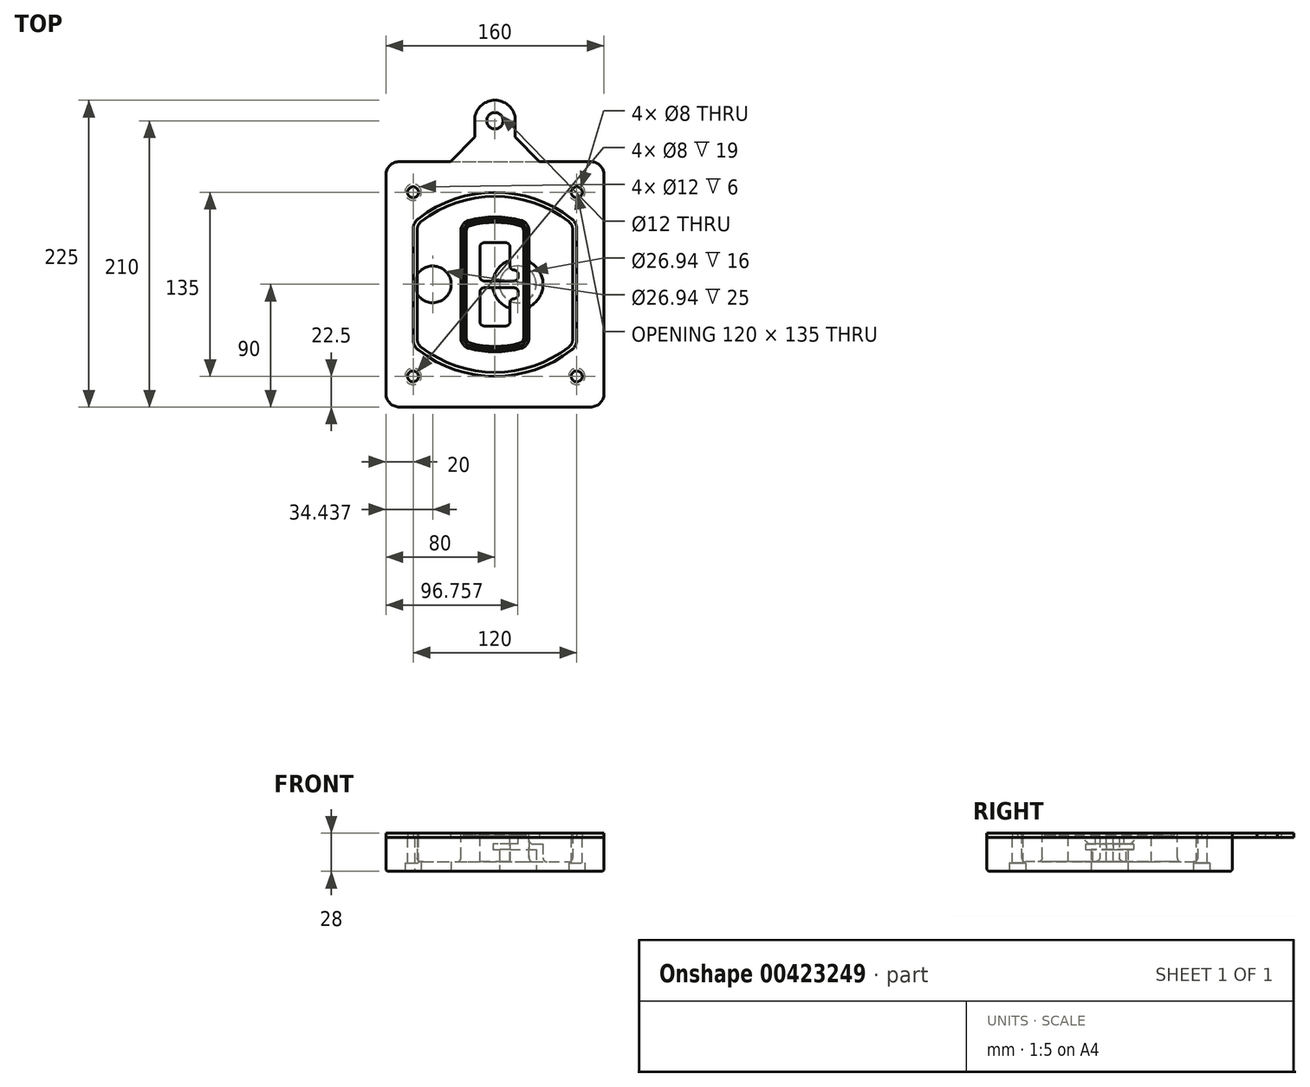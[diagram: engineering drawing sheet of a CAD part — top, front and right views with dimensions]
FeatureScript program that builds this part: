
annotation { "Feature Type Name" : "Feature", "Feature Type Description" : "" }
export const myFeature = defineFeature(function(context is Context, id is Id, definition is map)
    precondition{}
    {
        {
            var Q0;
            Q0=qCreatedBy(makeId("Top.planeOp"),FACE);
            var sketch = newSketch(context, id + "F0", { "sketchPlane" : qUnion([Q0])});
            skPoint(sketch, "E0.rect.middle", {"position": v(0, 0) * mm});
            skLineSegment(sketch, "E1.bottom", {"start": v(-70, -90) * mm, "end": v(70, -90) * mm});
            skLineSegment(sketch, "E1.top", {"start": v(-70, 90) * mm, "end": v(70, 90) * mm});
            skLineSegment(sketch, "E1.left", {"start": v(-80, -80) * mm, "end": v(-80, 80) * mm});
            skLineSegment(sketch, "E1.right", {"start": v(80, -80) * mm, "end": v(80, 80) * mm});
            skLineSegment(sketch, "E2", {"start": v(-80, 90) * mm, "end": v(80, -90) * mm, "construction": true});
            skLineSegment(sketch, "E3", {"start": v(80, 90) * mm, "end": v(-80, -90) * mm, "construction": true});
            skCircle(sketch, "E4", {"center": v(-60, 67.5) * mm, "radius": 4 * mm});
            skCircle(sketch, "E5", {"center": v(60, 67.5) * mm, "radius": 4 * mm});
            skCircle(sketch, "E6", {"center": v(60, -67.5) * mm, "radius": 4 * mm});
            skCircle(sketch, "E7", {"center": v(-60, -67.5) * mm, "radius": 4 * mm});
            skLineSegment(sketch, "E8", {"start": v(-60, 67.5) * mm, "end": v(60, 67.5) * mm, "construction": true});
            skLineSegment(sketch, "E9", {"start": v(60, 67.5) * mm, "end": v(60, -67.5) * mm, "construction": true});
            skLineSegment(sketch, "E10", {"start": v(60, -67.5) * mm, "end": v(-60, -67.5) * mm, "construction": true});
            skLineSegment(sketch, "E11", {"start": v(-60, -67.5) * mm, "end": v(-60, 67.5) * mm, "construction": true});
            skLineSegment(sketch, "E12", {"start": v(-60, 40.3) * mm, "end": v(-60, -40.3) * mm});
            skLineSegment(sketch, "E13", {"start": v(60, 40.3) * mm, "end": v(60, -40.3) * mm});
            skArc(sketch, "E14", {"start": v(56.15, 48.18) * mm, "mid": v(0, 67.5) * mm, "end": v(-56.15, 48.18) * mm});
            skArc(sketch, "E15", {"start": v(-56.15, -48.18) * mm, "mid": v(0, -67.5) * mm, "end": v(56.15, -48.18) * mm});
            skLineSegment(sketch, "E16", {"start": v(-60, 0) * mm, "end": v(60, 0) * mm, "construction": true});
            skPoint(sketch, "E17.visualSharp", {"position": v(-60, -45) * mm});
            skArc(sketch, "E17.filletArc", {"start": v(-60, -40.3) * mm, "mid": v(-58.99, -44.68) * mm, "end": v(-56.15, -48.18) * mm});
            skPoint(sketch, "E18.visualSharp", {"position": v(-60, 45) * mm});
            skArc(sketch, "E18.filletArc", {"start": v(-56.15, 48.18) * mm, "mid": v(-58.99, 44.68) * mm, "end": v(-60, 40.3) * mm});
            skPoint(sketch, "E19.visualSharp", {"position": v(60, 45) * mm});
            skArc(sketch, "E19.filletArc", {"start": v(60, 40.3) * mm, "mid": v(58.99, 44.68) * mm, "end": v(56.15, 48.18) * mm});
            skPoint(sketch, "E20.visualSharp", {"position": v(60, -45) * mm});
            skArc(sketch, "E20.filletArc", {"start": v(56.15, -48.18) * mm, "mid": v(58.99, -44.68) * mm, "end": v(60, -40.3) * mm});
            skPoint(sketch, "E21.visualSharp", {"position": v(-80, 90) * mm});
            skArc(sketch, "E21.filletArc", {"start": v(-70, 90) * mm, "mid": v(-77.07, 87.07) * mm, "end": v(-80, 80) * mm});
            skPoint(sketch, "E22.visualSharp", {"position": v(80, 90) * mm});
            skArc(sketch, "E22.filletArc", {"start": v(80, 80) * mm, "mid": v(77.07, 87.07) * mm, "end": v(70, 90) * mm});
            skPoint(sketch, "E23.visualSharp", {"position": v(80, -90) * mm});
            skArc(sketch, "E23.filletArc", {"start": v(70, -90) * mm, "mid": v(77.07, -87.07) * mm, "end": v(80, -80) * mm});
            skPoint(sketch, "E24.visualSharp", {"position": v(-80, -90) * mm});
            skArc(sketch, "E24.filletArc", {"start": v(-80, -80) * mm, "mid": v(-77.07, -87.07) * mm, "end": v(-70, -90) * mm});
            skArc(sketch, "E25.0", {"start": v(57, 40.3) * mm, "mid": v(56.3, 43.36) * mm, "end": v(54.3, 45.81) * mm});
            skLineSegment(sketch, "E25.1", {"start": v(57, 40.3) * mm, "end": v(57, -40.3) * mm});
            skArc(sketch, "E25.2", {"start": v(54.3, -45.81) * mm, "mid": v(56.3, -43.36) * mm, "end": v(57, -40.3) * mm});
            skArc(sketch, "E25.3", {"start": v(-54.3, -45.81) * mm, "mid": v(0, -64.5) * mm, "end": v(54.3, -45.81) * mm});
            skArc(sketch, "E25.4", {"start": v(-57, -40.3) * mm, "mid": v(-56.3, -43.36) * mm, "end": v(-54.3, -45.81) * mm});
            skArc(sketch, "E25.5", {"start": v(54.3, 45.81) * mm, "mid": v(0, 64.5) * mm, "end": v(-54.3, 45.81) * mm});
            skLineSegment(sketch, "E25.6", {"start": v(-57, 40.3) * mm, "end": v(-57, -40.3) * mm});
            skArc(sketch, "E25.7", {"start": v(-54.3, 45.81) * mm, "mid": v(-56.3, 43.36) * mm, "end": v(-57, 40.3) * mm});
            skArc(sketch, "E26.0", {"start": v(-58.62, 51.33) * mm, "mid": v(-62.58, 46.43) * mm, "end": v(-64, 40.3) * mm});
            skArc(sketch, "E26.1", {"start": v(58.62, 51.33) * mm, "mid": v(0, 71.5) * mm, "end": v(-58.62, 51.33) * mm});
            skArc(sketch, "E26.2", {"start": v(64, 40.3) * mm, "mid": v(62.58, 46.43) * mm, "end": v(58.62, 51.33) * mm});
            skLineSegment(sketch, "E26.3", {"start": v(64, 40.3) * mm, "end": v(64, -40.3) * mm});
            skArc(sketch, "E26.4", {"start": v(58.62, -51.33) * mm, "mid": v(62.58, -46.43) * mm, "end": v(64, -40.3) * mm});
            skLineSegment(sketch, "E26.5", {"start": v(-64, 40.3) * mm, "end": v(-64, -40.3) * mm});
            skArc(sketch, "E26.6", {"start": v(-58.62, -51.33) * mm, "mid": v(0, -71.5) * mm, "end": v(58.62, -51.33) * mm});
            skArc(sketch, "E26.7", {"start": v(-64, -40.3) * mm, "mid": v(-62.58, -46.43) * mm, "end": v(-58.62, -51.33) * mm});
            skSolve(sketch);
        }
        {
            var Q0;
            Q0=makeQuery(id+"F0.imprint","IMPRINT",FACE,{"disambiguationData":[TD([[makeQuery(id+"F0.imprint","IMPRINT",EDGE,{"derivedFrom":sQuery(id+"F0.wireOp",EDGE,"E1.bottom")}),1.0]])]});
            var Q1;
            Q1=makeQuery(id+"F0.imprint","IMPRINT",FACE,{"disambiguationData":[TD([[makeQuery(id+"F0.imprint","IMPRINT",EDGE,{"derivedFrom":sQuery(id+"F0.wireOp",EDGE,"E12")}),1.0]])]});
            var Q2;
            Q2=makeQuery(id+"F0.imprint","IMPRINT",FACE,{"disambiguationData":[TD([[makeQuery(id+"F0.imprint","IMPRINT",EDGE,{"derivedFrom":sQuery(id+"F0.wireOp",EDGE,"E25.0")}),1.0]])]});
            var Q3;
            Q3=makeQuery(id+"F0.imprint","IMPRINT",FACE,{"disambiguationData":[TD([[makeQuery(id+"F0.imprint","IMPRINT",EDGE,{"derivedFrom":sQuery(id+"F0.wireOp",EDGE,"E12")}),-1.0]])]});
            extrude(context, id + "F1", {"entities" : qUnion([Q0, Q1, Q2, Q3]), "oppositeDirection" : true, "depth" : 25 * mm});
        }
        {
            var Q0;
            Q0=makeQuery(id+"F0.imprint","IMPRINT",FACE,{"disambiguationData":[TD([[makeQuery(id+"F0.imprint","IMPRINT",EDGE,{"derivedFrom":sQuery(id+"F0.wireOp",EDGE,"E12")}),1.0]])]});
            extrude(context, id + "F2", {"entities" : qUnion([Q0]), "operationType" : NewBodyOperationType.ADD, "depth" : 3 * mm});
        }
        {
            var Q0;
            Q0=makeQuery(id+"F0.imprint","IMPRINT",FACE,{"disambiguationData":[TD([[makeQuery(id+"F0.imprint","IMPRINT",EDGE,{"derivedFrom":sQuery(id+"F0.wireOp",EDGE,"E25.0")}),1.0]])]});
            extrude(context, id + "F3", {"entities" : qUnion([Q0]), "operationType" : NewBodyOperationType.REMOVE, "oppositeDirection" : true, "depth" : 18 * mm});
        }
        {
            var Q0;
            Q0=makeQuery(id+"F2.opExtrude","CAP_FACE",FACE,{"disambiguationData":[OSD([sQuery(id+"F0.wireOp",EDGE,"E12"),sQuery(id+"F0.wireOp",EDGE,"E13"),sQuery(id+"F0.wireOp",EDGE,"E14"),sQuery(id+"F0.wireOp",EDGE,"E15"),sQuery(id+"F0.wireOp",EDGE,"E17.filletArc"),sQuery(id+"F0.wireOp",EDGE,"E18.filletArc"),sQuery(id+"F0.wireOp",EDGE,"E19.filletArc"),sQuery(id+"F0.wireOp",EDGE,"E20.filletArc"),sQuery(id+"F0.wireOp",EDGE,"E25.0"),sQuery(id+"F0.wireOp",EDGE,"E25.1"),sQuery(id+"F0.wireOp",EDGE,"E25.2"),sQuery(id+"F0.wireOp",EDGE,"E25.3"),sQuery(id+"F0.wireOp",EDGE,"E25.4"),sQuery(id+"F0.wireOp",EDGE,"E25.5"),sQuery(id+"F0.wireOp",EDGE,"E25.6"),sQuery(id+"F0.wireOp",EDGE,"E25.7")])],"isStart":false});
            var sketch = newSketch(context, id + "F4", { "sketchPlane" : qUnion([Q0])});
            skArc(sketch, "E27.0", {"start": v(-19.08, -46.97) * mm, "mid": v(0, -49.5) * mm, "end": v(19.08, -46.97) * mm});
            skArc(sketch, "E28.0", {"start": v(19.08, 46.97) * mm, "mid": v(0, 49.5) * mm, "end": v(-19.08, 46.97) * mm});
            skLineSegment(sketch, "E29", {"start": v(-25, 39.25) * mm, "end": v(-25, -39.25) * mm});
            skLineSegment(sketch, "E30", {"start": v(25, 39.25) * mm, "end": v(25, -39.25) * mm});
            skLineSegment(sketch, "E31", {"start": v(-25, 45.1) * mm, "end": v(25, 45.1) * mm, "construction": true});
            skLineSegment(sketch, "E32", {"start": v(-25, -45.1) * mm, "end": v(25, -45.1) * mm, "construction": true});
            skPoint(sketch, "E33.visualSharp", {"position": v(-25, 45.1) * mm});
            skArc(sketch, "E33.filletArc", {"start": v(-19.08, 46.97) * mm, "mid": v(-23.35, 44.11) * mm, "end": v(-25, 39.25) * mm});
            skPoint(sketch, "E34.visualSharp", {"position": v(25, 45.1) * mm});
            skArc(sketch, "E34.filletArc", {"start": v(25, 39.25) * mm, "mid": v(23.35, 44.11) * mm, "end": v(19.08, 46.97) * mm});
            skPoint(sketch, "E35.visualSharp", {"position": v(25, -45.1) * mm});
            skArc(sketch, "E35.filletArc", {"start": v(19.08, -46.97) * mm, "mid": v(23.35, -44.11) * mm, "end": v(25, -39.25) * mm});
            skPoint(sketch, "E36.visualSharp", {"position": v(-25, -45.1) * mm});
            skArc(sketch, "E36.filletArc", {"start": v(-25, -39.25) * mm, "mid": v(-23.35, -44.11) * mm, "end": v(-19.08, -46.97) * mm});
            skArc(sketch, "E37.0", {"start": v(54.3, 45.81) * mm, "mid": v(0, 64.5) * mm, "end": v(-54.3, 45.81) * mm});
            skArc(sketch, "E37.1", {"start": v(-54.3, 45.81) * mm, "mid": v(-56.3, 43.36) * mm, "end": v(-57, 40.3) * mm});
            skLineSegment(sketch, "E37.2", {"start": v(-57, 40.3) * mm, "end": v(-57, -40.3) * mm});
            skArc(sketch, "E37.3", {"start": v(-57, -40.3) * mm, "mid": v(-56.3, -43.36) * mm, "end": v(-54.3, -45.81) * mm});
            skArc(sketch, "E37.4", {"start": v(-54.3, -45.81) * mm, "mid": v(0, -64.5) * mm, "end": v(54.3, -45.81) * mm});
            skArc(sketch, "E37.5", {"start": v(54.3, -45.81) * mm, "mid": v(56.3, -43.36) * mm, "end": v(57, -40.3) * mm});
            skLineSegment(sketch, "E37.6", {"start": v(57, 40.3) * mm, "end": v(57, -40.3) * mm});
            skArc(sketch, "E37.7", {"start": v(57, 40.3) * mm, "mid": v(56.3, 43.36) * mm, "end": v(54.3, 45.81) * mm});
            skLineSegment(sketch, "E38.0", {"start": v(23, 39.25) * mm, "end": v(23, -39.25) * mm});
            skArc(sketch, "E38.1", {"start": v(18.56, -45.04) * mm, "mid": v(21.76, -42.9) * mm, "end": v(23, -39.25) * mm});
            skArc(sketch, "E38.2", {"start": v(-18.56, -45.04) * mm, "mid": v(0, -47.5) * mm, "end": v(18.56, -45.04) * mm});
            skArc(sketch, "E38.3", {"start": v(-23, -39.25) * mm, "mid": v(-21.76, -42.9) * mm, "end": v(-18.56, -45.04) * mm});
            skLineSegment(sketch, "E38.4", {"start": v(-23, 39.25) * mm, "end": v(-23, -39.25) * mm});
            skArc(sketch, "E38.5", {"start": v(23, 39.25) * mm, "mid": v(21.76, 42.9) * mm, "end": v(18.56, 45.04) * mm});
            skArc(sketch, "E38.6", {"start": v(-18.56, 45.04) * mm, "mid": v(-21.76, 42.9) * mm, "end": v(-23, 39.25) * mm});
            skArc(sketch, "E38.7", {"start": v(18.56, 45.04) * mm, "mid": v(0, 47.5) * mm, "end": v(-18.56, 45.04) * mm});
            skArc(sketch, "E39.0", {"start": v(21, 39.25) * mm, "mid": v(20.18, 41.68) * mm, "end": v(18.04, 43.1) * mm});
            skLineSegment(sketch, "E39.1", {"start": v(21, 39.25) * mm, "end": v(21, -39.25) * mm});
            skArc(sketch, "E39.2", {"start": v(18.04, -43.1) * mm, "mid": v(20.18, -41.68) * mm, "end": v(21, -39.25) * mm});
            skArc(sketch, "E39.3", {"start": v(-18.04, -43.1) * mm, "mid": v(0, -45.5) * mm, "end": v(18.04, -43.1) * mm});
            skArc(sketch, "E39.4", {"start": v(-21, -39.25) * mm, "mid": v(-20.18, -41.68) * mm, "end": v(-18.04, -43.1) * mm});
            skArc(sketch, "E39.5", {"start": v(18.04, 43.1) * mm, "mid": v(0, 45.5) * mm, "end": v(-18.04, 43.1) * mm});
            skLineSegment(sketch, "E39.6", {"start": v(-21, 39.25) * mm, "end": v(-21, -39.25) * mm});
            skArc(sketch, "E39.7", {"start": v(-18.04, 43.1) * mm, "mid": v(-20.18, 41.68) * mm, "end": v(-21, 39.25) * mm});
            skLineSegment(sketch, "E40", {"start": v(-25, 0) * mm, "end": v(25, 0) * mm, "construction": true});
            skLineSegment(sketch, "E41", {"start": v(-11, 5.5) * mm, "end": v(-11, 27.5) * mm});
            skLineSegment(sketch, "E42", {"start": v(-8, 30.5) * mm, "end": v(8, 30.5) * mm});
            skLineSegment(sketch, "E43", {"start": v(11, 27.5) * mm, "end": v(11, 13.5) * mm});
            skLineSegment(sketch, "E44", {"start": v(14, 10.5) * mm, "end": v(14, 10.5) * mm});
            skLineSegment(sketch, "E45", {"start": v(17, 7.5) * mm, "end": v(17, 5.5) * mm});
            skLineSegment(sketch, "E46", {"start": v(14, 2.5) * mm, "end": v(-8, 2.5) * mm});
            skPoint(sketch, "E47.visualSharp", {"position": v(-11, 30.5) * mm});
            skArc(sketch, "E47.filletArc", {"start": v(-8, 30.5) * mm, "mid": v(-10.12, 29.62) * mm, "end": v(-11, 27.5) * mm});
            skPoint(sketch, "E48.visualSharp", {"position": v(11, 30.5) * mm});
            skArc(sketch, "E48.filletArc", {"start": v(11, 27.5) * mm, "mid": v(10.12, 29.62) * mm, "end": v(8, 30.5) * mm});
            skPoint(sketch, "E49.visualSharp", {"position": v(11, 10.5) * mm});
            skArc(sketch, "E49.filletArc", {"start": v(11, 13.5) * mm, "mid": v(11.88, 11.38) * mm, "end": v(14, 10.5) * mm});
            skPoint(sketch, "E50.visualSharp", {"position": v(17, 10.5) * mm});
            skArc(sketch, "E50.filletArc", {"start": v(17, 7.5) * mm, "mid": v(16.12, 9.62) * mm, "end": v(14, 10.5) * mm});
            skPoint(sketch, "E51.visualSharp", {"position": v(17, 2.5) * mm});
            skArc(sketch, "E51.filletArc", {"start": v(14, 2.5) * mm, "mid": v(16.12, 3.38) * mm, "end": v(17, 5.5) * mm});
            skPoint(sketch, "E52.visualSharp", {"position": v(-11, 2.5) * mm});
            skArc(sketch, "E52.filletArc", {"start": v(-11, 5.5) * mm, "mid": v(-10.12, 3.38) * mm, "end": v(-8, 2.5) * mm});
            skLineSegment(sketch, "E53.0.MirrorCS", {"start": v(14, -2.5) * mm, "end": v(-8, -2.5) * mm});
            skArc(sketch, "E54.0.MirrorCS", {"start": v(-11, -5.5) * mm, "mid": v(-10.12, -3.38) * mm, "end": v(-8, -2.5) * mm});
            skLineSegment(sketch, "E55.0.MirrorCS", {"start": v(-11, -5.5) * mm, "end": v(-11, -27.5) * mm});
            skArc(sketch, "E56.0.MirrorCS", {"start": v(-8, -30.5) * mm, "mid": v(-10.12, -29.62) * mm, "end": v(-11, -27.5) * mm});
            skLineSegment(sketch, "E57.0.MirrorCS", {"start": v(-8, -30.5) * mm, "end": v(8, -30.5) * mm});
            skArc(sketch, "E58.0.MirrorCS", {"start": v(11, -27.5) * mm, "mid": v(10.12, -29.62) * mm, "end": v(8, -30.5) * mm});
            skLineSegment(sketch, "E59.0.MirrorCS", {"start": v(11, -27.5) * mm, "end": v(11, -13.5) * mm});
            skArc(sketch, "E60.0.MirrorCS", {"start": v(11, -13.5) * mm, "mid": v(11.88, -11.38) * mm, "end": v(14, -10.5) * mm});
            skArc(sketch, "E61.0.MirrorCS", {"start": v(17, -7.5) * mm, "mid": v(16.12, -9.62) * mm, "end": v(14, -10.5) * mm});
            skLineSegment(sketch, "E62.0.MirrorCS", {"start": v(17, -7.5) * mm, "end": v(17, -5.5) * mm});
            skArc(sketch, "E63.0.MirrorCS", {"start": v(14, -2.5) * mm, "mid": v(16.12, -3.38) * mm, "end": v(17, -5.5) * mm});
            skSolve(sketch);
        }
        {
            var Q0;
            Q0=makeQuery(id+"F4.imprint","IMPRINT",FACE,{"disambiguationData":[TD([[makeQuery(id+"F4.imprint","IMPRINT",EDGE,{"derivedFrom":sQuery(id+"F4.wireOp",EDGE,"E27.0")}),1.0]])]});
            var Q1;
            Q1=makeQuery(id+"F4.imprint","IMPRINT",FACE,{"disambiguationData":[TD([[makeQuery(id+"F4.imprint","IMPRINT",EDGE,{"derivedFrom":sQuery(id+"F4.wireOp",EDGE,"E38.0")}),-1.0]])]});
            var Q2;
            Q2=makeQuery(id+"F4.imprint","IMPRINT",FACE,{"disambiguationData":[TD([[makeQuery(id+"F4.imprint","IMPRINT",EDGE,{"derivedFrom":sQuery(id+"F4.wireOp",EDGE,"E39.0")}),1.0]])]});
            extrude(context, id + "F5", {"entities" : qUnion([Q0, Q1, Q2]), "operationType" : NewBodyOperationType.ADD, "endBound" : BoundingType.UP_TO_NEXT, "oppositeDirection" : true, "depth" : 25 * mm});
        }
        {
            var Q0;
            Q0=makeQuery(id+"F4.imprint","IMPRINT",FACE,{"disambiguationData":[TD([[makeQuery(id+"F4.imprint","IMPRINT",EDGE,{"derivedFrom":sQuery(id+"F4.wireOp",EDGE,"E38.0")}),-1.0]])]});
            extrude(context, id + "F6", {"entities" : qUnion([Q0]), "operationType" : NewBodyOperationType.REMOVE, "oppositeDirection" : true, "depth" : 2 * mm});
        }
        {
            var Q0;
            Q0=makeQuery(id+"F1.opExtrude","CAP_FACE",FACE,{"disambiguationData":[OSD([sQuery(id+"F0.wireOp",EDGE,"E1.bottom"),sQuery(id+"F0.wireOp",EDGE,"E1.top"),sQuery(id+"F0.wireOp",EDGE,"E1.left"),sQuery(id+"F0.wireOp",EDGE,"E1.right"),sQuery(id+"F0.wireOp",EDGE,"E4"),sQuery(id+"F0.wireOp",EDGE,"E5"),sQuery(id+"F0.wireOp",EDGE,"E6"),sQuery(id+"F0.wireOp",EDGE,"E7"),sQuery(id+"F0.wireOp",EDGE,"E21.filletArc"),sQuery(id+"F0.wireOp",EDGE,"E22.filletArc"),sQuery(id+"F0.wireOp",EDGE,"E23.filletArc"),sQuery(id+"F0.wireOp",EDGE,"E24.filletArc")])],"isStart":false});
            var sketch = newSketch(context, id + "F7", { "sketchPlane" : qUnion([Q0])});
            skCircle(sketch, "E64", {"center": v(16.76, 0) * mm, "radius": 13.47 * mm});
            skCircle(sketch, "E65", {"center": v(-45.56, 0) * mm, "radius": 13.47 * mm});
            skLineSegment(sketch, "E66", {"start": v(80, 0) * mm, "end": v(-80, 0) * mm});
            skCircle(sketch, "E67", {"center": v(16.76, 0) * mm, "radius": 18.47 * mm});
            skCircle(sketch, "E68", {"center": v(60, -67.5) * mm, "radius": 6 * mm});
            skCircle(sketch, "E69", {"center": v(-60, -67.5) * mm, "radius": 6 * mm});
            skCircle(sketch, "E70", {"center": v(-60, 67.5) * mm, "radius": 6 * mm});
            skCircle(sketch, "E71", {"center": v(60, 67.5) * mm, "radius": 6 * mm});
            skSolve(sketch);
        }
        {
            var Q0;
            {var subQ1=sQuery(id+"F7.wireOp",EDGE,"E66");var subQ4=sQuery(id+"F7.wireOp",EDGE,"E64");var subQ6=makeQuery(id+"F7.imprint","INTERSECT",VERTEX,{"disambiguationData":[OD(0.0)],"derivedFrom":[subQ4,subQ1]});Q0=makeQuery(id+"F7.imprint","IMPRINT",FACE,{"disambiguationData":[TD([[makeQuery(id+"F7.imprint","IMPRINT",EDGE,{"disambiguationData":[TD([[subQ6,-1.0]])],"derivedFrom":subQ4}),-1.0]])]});}
            var Q1;
            {var subQ0=sQuery(id+"F7.wireOp",EDGE,"E66");var subQ1=sQuery(id+"F7.wireOp",EDGE,"E64");var subQ3=makeQuery(id+"F7.imprint","INTERSECT",VERTEX,{"disambiguationData":[OD(0.0)],"derivedFrom":[subQ1,subQ0]});Q1=makeQuery(id+"F7.imprint","IMPRINT",FACE,{"disambiguationData":[TD([[makeQuery(id+"F7.imprint","IMPRINT",EDGE,{"disambiguationData":[TD([[subQ3,-1.0]])],"derivedFrom":subQ1}),1.0]])]});}
            var Q2;
            {var subQ0=sQuery(id+"F7.wireOp",EDGE,"E66");var subQ1=sQuery(id+"F7.wireOp",EDGE,"E64");var subQ3=makeQuery(id+"F7.imprint","INTERSECT",VERTEX,{"disambiguationData":[OD(0.0)],"derivedFrom":[subQ1,subQ0]});Q2=makeQuery(id+"F7.imprint","IMPRINT",FACE,{"disambiguationData":[TD([[makeQuery(id+"F7.imprint","IMPRINT",EDGE,{"disambiguationData":[TD([[subQ3,1.0]])],"derivedFrom":subQ1}),1.0]])]});}
            var Q3;
            {var subQ1=sQuery(id+"F7.wireOp",EDGE,"E66");var subQ4=sQuery(id+"F7.wireOp",EDGE,"E64");var subQ6=makeQuery(id+"F7.imprint","INTERSECT",VERTEX,{"disambiguationData":[OD(0.0)],"derivedFrom":[subQ4,subQ1]});Q3=makeQuery(id+"F7.imprint","IMPRINT",FACE,{"disambiguationData":[TD([[makeQuery(id+"F7.imprint","IMPRINT",EDGE,{"disambiguationData":[TD([[subQ6,1.0]])],"derivedFrom":subQ4}),-1.0]])]});}
            extrude(context, id + "F8", {"entities" : qUnion([Q0, Q1, Q2, Q3]), "operationType" : NewBodyOperationType.ADD, "oppositeDirection" : true, "depth" : 20 * mm});
        }
        {
            var Q0;
            {var subQ0=sQuery(id+"F7.wireOp",EDGE,"E66");var subQ1=sQuery(id+"F7.wireOp",EDGE,"E64");var subQ3=makeQuery(id+"F7.imprint","INTERSECT",VERTEX,{"disambiguationData":[OD(0.0)],"derivedFrom":[subQ1,subQ0]});Q0=makeQuery(id+"F7.imprint","IMPRINT",FACE,{"disambiguationData":[TD([[makeQuery(id+"F7.imprint","IMPRINT",EDGE,{"disambiguationData":[TD([[subQ3,-1.0]])],"derivedFrom":subQ1}),1.0]])]});}
            var Q1;
            {var subQ0=sQuery(id+"F7.wireOp",EDGE,"E66");var subQ1=sQuery(id+"F7.wireOp",EDGE,"E64");var subQ3=makeQuery(id+"F7.imprint","INTERSECT",VERTEX,{"disambiguationData":[OD(0.0)],"derivedFrom":[subQ1,subQ0]});Q1=makeQuery(id+"F7.imprint","IMPRINT",FACE,{"disambiguationData":[TD([[makeQuery(id+"F7.imprint","IMPRINT",EDGE,{"disambiguationData":[TD([[subQ3,1.0]])],"derivedFrom":subQ1}),1.0]])]});}
            extrude(context, id + "F9", {"entities" : qUnion([Q0, Q1]), "operationType" : NewBodyOperationType.REMOVE, "oppositeDirection" : true, "depth" : 16 * mm});
        }
        {
            var Q0;
            {var subQ0=sQuery(id+"F7.wireOp",EDGE,"E66");var subQ1=sQuery(id+"F7.wireOp",EDGE,"E65");var subQ3=makeQuery(id+"F7.imprint","INTERSECT",VERTEX,{"disambiguationData":[OD(0.0)],"derivedFrom":[subQ1,subQ0]});Q0=makeQuery(id+"F7.imprint","IMPRINT",FACE,{"disambiguationData":[TD([[makeQuery(id+"F7.imprint","IMPRINT",EDGE,{"disambiguationData":[TD([[subQ3,-1.0]])],"derivedFrom":subQ1}),1.0]])]});}
            var Q1;
            {var subQ0=sQuery(id+"F7.wireOp",EDGE,"E66");var subQ1=sQuery(id+"F7.wireOp",EDGE,"E65");var subQ3=makeQuery(id+"F7.imprint","INTERSECT",VERTEX,{"disambiguationData":[OD(0.0)],"derivedFrom":[subQ1,subQ0]});Q1=makeQuery(id+"F7.imprint","IMPRINT",FACE,{"disambiguationData":[TD([[makeQuery(id+"F7.imprint","IMPRINT",EDGE,{"disambiguationData":[TD([[subQ3,1.0]])],"derivedFrom":subQ1}),1.0]])]});}
            extrude(context, id + "F10", {"entities" : qUnion([Q0, Q1]), "operationType" : NewBodyOperationType.REMOVE, "oppositeDirection" : true, "depth" : 25 * mm});
        }
        {
            var Q0;
            Q0=makeQuery(id+"F7.imprint","IMPRINT",FACE,{"disambiguationData":[TD([[makeQuery(id+"F7.imprint","IMPRINT",EDGE,{"derivedFrom":sQuery(id+"F7.wireOp",EDGE,"E68")}),1.0]])]});
            var Q1;
            Q1=makeQuery(id+"F7.imprint","IMPRINT",FACE,{"disambiguationData":[TD([[makeQuery(id+"F7.imprint","IMPRINT",EDGE,{"derivedFrom":makeQuery(id+"F1.opExtrude","CAP_EDGE",EDGE,{"disambiguationData":[OSD([sQuery(id+"F0.wireOp",EDGE,"E5")])],"isStart":false})}),-1.0]])]});
            var Q2;
            Q2=makeQuery(id+"F7.imprint","IMPRINT",FACE,{"disambiguationData":[TD([[makeQuery(id+"F7.imprint","IMPRINT",EDGE,{"derivedFrom":sQuery(id+"F7.wireOp",EDGE,"E69")}),1.0]])]});
            var Q3;
            Q3=makeQuery(id+"F7.imprint","IMPRINT",FACE,{"disambiguationData":[TD([[makeQuery(id+"F7.imprint","IMPRINT",EDGE,{"derivedFrom":makeQuery(id+"F1.opExtrude","CAP_EDGE",EDGE,{"disambiguationData":[OSD([sQuery(id+"F0.wireOp",EDGE,"E4")])],"isStart":false})}),-1.0]])]});
            var Q4;
            Q4=makeQuery(id+"F7.imprint","IMPRINT",FACE,{"disambiguationData":[TD([[makeQuery(id+"F7.imprint","IMPRINT",EDGE,{"derivedFrom":sQuery(id+"F7.wireOp",EDGE,"E70")}),1.0]])]});
            var Q5;
            Q5=makeQuery(id+"F7.imprint","IMPRINT",FACE,{"disambiguationData":[TD([[makeQuery(id+"F7.imprint","IMPRINT",EDGE,{"derivedFrom":makeQuery(id+"F1.opExtrude","CAP_EDGE",EDGE,{"disambiguationData":[OSD([sQuery(id+"F0.wireOp",EDGE,"E7")])],"isStart":false})}),-1.0]])]});
            var Q6;
            Q6=makeQuery(id+"F7.imprint","IMPRINT",FACE,{"disambiguationData":[TD([[makeQuery(id+"F7.imprint","IMPRINT",EDGE,{"derivedFrom":sQuery(id+"F7.wireOp",EDGE,"E71")}),1.0]])]});
            var Q7;
            Q7=makeQuery(id+"F7.imprint","IMPRINT",FACE,{"disambiguationData":[TD([[makeQuery(id+"F7.imprint","IMPRINT",EDGE,{"derivedFrom":makeQuery(id+"F1.opExtrude","CAP_EDGE",EDGE,{"disambiguationData":[OSD([sQuery(id+"F0.wireOp",EDGE,"E6")])],"isStart":false})}),-1.0]])]});
            extrude(context, id + "F11", {"entities" : qUnion([Q0, Q1, Q2, Q3, Q4, Q5, Q6, Q7]), "operationType" : NewBodyOperationType.REMOVE, "oppositeDirection" : true, "depth" : 6 * mm});
        }
        {
            var Q0;
            Q0=makeQuery(id+"F9.boolean.opBoolean","COPY",FACE,{"derivedFrom":makeQuery(id+"F9.opExtrude","CAP_FACE",FACE,{"disambiguationData":[OSD([sQuery(id+"F7.wireOp",EDGE,"E64")])],"isStart":false})});
            var sketch = newSketch(context, id + "F12", { "sketchPlane" : qUnion([Q0])});
            skArc(sketch, "E72.0", {"start": v(11, 17.55) * mm, "mid": v(2.57, 11.82) * mm, "end": v(-1.54, 2.5) * mm});
            skArc(sketch, "E72.1", {"start": v(-1.54, -2.5) * mm, "mid": v(2.57, -11.82) * mm, "end": v(11, -17.55) * mm});
            skLineSegment(sketch, "E73", {"start": v(-1.54, -2.5) * mm, "end": v(14, -2.5) * mm});
            skLineSegment(sketch, "E74.0", {"start": v(14, 2.5) * mm, "end": v(-1.54, 2.5) * mm});
            skArc(sketch, "E74.1", {"start": v(14, 2.5) * mm, "mid": v(16.12, 3.38) * mm, "end": v(17, 5.5) * mm});
            skLineSegment(sketch, "E74.2", {"start": v(17, 7.5) * mm, "end": v(17, 5.5) * mm});
            skArc(sketch, "E74.3", {"start": v(17, 7.5) * mm, "mid": v(16.12, 9.62) * mm, "end": v(14, 10.5) * mm});
            skArc(sketch, "E74.4", {"start": v(11, 13.5) * mm, "mid": v(11.88, 11.38) * mm, "end": v(14, 10.5) * mm});
            skLineSegment(sketch, "E74.5", {"start": v(11, 17.55) * mm, "end": v(11, 13.5) * mm});
            skLineSegment(sketch, "E74.7", {"start": v(14, -2.5) * mm, "end": v(-1.54, -2.5) * mm});
            skArc(sketch, "E74.8", {"start": v(14, -2.5) * mm, "mid": v(16.12, -3.38) * mm, "end": v(17, -5.5) * mm});
            skLineSegment(sketch, "E74.9", {"start": v(17, -7.5) * mm, "end": v(17, -5.5) * mm});
            skArc(sketch, "E74.10", {"start": v(17, -7.5) * mm, "mid": v(16.12, -9.62) * mm, "end": v(14, -10.5) * mm});
            skArc(sketch, "E74.11", {"start": v(11, -13.5) * mm, "mid": v(11.88, -11.38) * mm, "end": v(14, -10.5) * mm});
            skLineSegment(sketch, "E74.12", {"start": v(11, -17.55) * mm, "end": v(11, -13.5) * mm});
            skPoint(sketch, "E75.orphan", {"position": v(11, -27.5) * mm});
            skPoint(sketch, "E76.orphan", {"position": v(-8, -2.5) * mm});
            skPoint(sketch, "E77.orphan", {"position": v(-8, 2.5) * mm});
            skPoint(sketch, "E78.orphan", {"position": v(11, 27.5) * mm});
            skSolve(sketch);
        }
        {
            var Q0;
            {var subQ7=sQuery(id+"F12.wireOp",EDGE,"E72.0");var subQ14=sQuery(id+"F12.wireOp",EDGE,"E72.1");var subQ16=sQuery(id+"F12.wireOp",EDGE,"E74.1");var subQ18=sQuery(id+"F12.wireOp",EDGE,"E74.8");Q0=qUnion([makeQuery(id+"F12.imprint","IMPRINT",FACE,{"disambiguationData":[TD([[makeQuery(id+"F12.imprint","IMPRINT",EDGE,{"derivedFrom":subQ7}),1.0]])]}),makeQuery(id+"F12.imprint","IMPRINT",FACE,{"disambiguationData":[TD([[makeQuery(id+"F12.imprint","IMPRINT",EDGE,{"derivedFrom":subQ14}),1.0]])]}),makeQuery(id+"F12.imprint","IMPRINT",FACE,{"disambiguationData":[TD([[makeQuery(id+"F12.imprint","IMPRINT",EDGE,{"derivedFrom":subQ16}),1.0]])]}),makeQuery(id+"F12.imprint","IMPRINT",FACE,{"disambiguationData":[TD([[makeQuery(id+"F12.imprint","IMPRINT",EDGE,{"derivedFrom":subQ18}),-1.0]])]})]);}
            var Q1;
            Q1=makeQuery(id+"F5.boolean.opBoolean","SPLIT",FACE,{"disambiguationData":[TD([makeQuery(id+"F5.opExtrude","SWEPT_FACE",FACE,{"disambiguationData":[OSD([sQuery(id+"F4.wireOp",EDGE,"E41")])]})])],"derivedFrom":makeQuery(id+"F3.boolean.opBoolean","COPY",FACE,{"derivedFrom":makeQuery(id+"F3.opExtrude","CAP_FACE",FACE,{"disambiguationData":[OSD([sQuery(id+"F0.wireOp",EDGE,"E25.0"),sQuery(id+"F0.wireOp",EDGE,"E25.1"),sQuery(id+"F0.wireOp",EDGE,"E25.2"),sQuery(id+"F0.wireOp",EDGE,"E25.3"),sQuery(id+"F0.wireOp",EDGE,"E25.4"),sQuery(id+"F0.wireOp",EDGE,"E25.5"),sQuery(id+"F0.wireOp",EDGE,"E25.6"),sQuery(id+"F0.wireOp",EDGE,"E25.7")])],"isStart":false})})});
            extrude(context, id + "F13", {"entities" : qUnion([Q0]), "operationType" : NewBodyOperationType.REMOVE, "endBound" : BoundingType.UP_TO_SURFACE, "endBoundEntityFace" : qUnion([Q1]), "depth" : 25 * mm});
        }
        {
            var Q0;
            Q0=makeQuery(id+"F3.boolean.opBoolean","COPY",EDGE,{"derivedFrom":makeQuery(id+"F3.opExtrude","CAP_EDGE",EDGE,{"disambiguationData":[OSD([sQuery(id+"F0.wireOp",EDGE,"E25.6")])],"isStart":false})});
            var Q1;
            Q1=makeQuery(id+"F8.boolean.opBoolean","INTERSECT",EDGE,{"derivedFrom":[makeQuery(id+"F5.opExtrude","SWEPT_FACE",FACE,{"disambiguationData":[OSD([sQuery(id+"F4.wireOp",EDGE,"E30")])]}),makeQuery(id+"F8.opExtrude","CAP_FACE",FACE,{"disambiguationData":[OSD([sQuery(id+"F7.wireOp",EDGE,"E67")])],"isStart":false})]});
            var Q2;
            Q2=makeQuery(id+"F8.boolean.opBoolean","INTERSECT",EDGE,{"disambiguationData":[OD(1.0)],"derivedFrom":[makeQuery(id+"F5.opExtrude","SWEPT_FACE",FACE,{"disambiguationData":[OSD([sQuery(id+"F4.wireOp",EDGE,"E30")])]}),makeQuery(id+"F8.opExtrude","SWEPT_FACE",FACE,{"disambiguationData":[OSD([sQuery(id+"F7.wireOp",EDGE,"E67")])]})]});
            var Q3;
            {var subQ0=sQuery(id+"F4.wireOp",EDGE,"E30");Q3=makeQuery(id+"F8.boolean.opBoolean","SPLIT",EDGE,{"disambiguationData":[TD([makeQuery(id+"F5.opExtrude","SWEPT_FACE",FACE,{"disambiguationData":[OSD([sQuery(id+"F4.wireOp",EDGE,"E35.filletArc")])]})])],"derivedFrom":makeQuery(id+"F5.opExtrude","CAP_EDGE",EDGE,{"disambiguationData":[OSD([subQ0])],"isStart":false})});}
            var Q4;
            {var subQ0=sQuery(id+"F0.wireOp",EDGE,"E25.7");var subQ1=sQuery(id+"F0.wireOp",EDGE,"E25.1");var subQ2=sQuery(id+"F0.wireOp",EDGE,"E25.6");var subQ3=sQuery(id+"F0.wireOp",EDGE,"E25.5");var subQ4=sQuery(id+"F0.wireOp",EDGE,"E25.4");var subQ5=sQuery(id+"F0.wireOp",EDGE,"E25.0");var subQ6=sQuery(id+"F0.wireOp",EDGE,"E25.2");var subQ7=sQuery(id+"F0.wireOp",EDGE,"E25.3");Q4=makeQuery(id+"F8.boolean.opBoolean","INTERSECT",EDGE,{"derivedFrom":[makeQuery(id+"F5.boolean.opBoolean","SPLIT",FACE,{"disambiguationData":[TD([makeQuery(id+"F2.opExtrude","SWEPT_FACE",FACE,{"disambiguationData":[OSD([subQ5])]})])],"derivedFrom":makeQuery(id+"F3.boolean.opBoolean","COPY",FACE,{"derivedFrom":makeQuery(id+"F3.opExtrude","CAP_FACE",FACE,{"disambiguationData":[OSD([subQ5,subQ1,subQ6,subQ7,subQ4,subQ3,subQ2,subQ0])],"isStart":false})})}),makeQuery(id+"F8.opExtrude","SWEPT_FACE",FACE,{"disambiguationData":[OSD([sQuery(id+"F7.wireOp",EDGE,"E67")])]})]});}
            var Q5;
            Q5=makeQuery(id+"F8.boolean.opBoolean","INTERSECT",EDGE,{"disambiguationData":[OD(0.0)],"derivedFrom":[makeQuery(id+"F5.opExtrude","SWEPT_FACE",FACE,{"disambiguationData":[OSD([sQuery(id+"F4.wireOp",EDGE,"E30")])]}),makeQuery(id+"F8.opExtrude","SWEPT_FACE",FACE,{"disambiguationData":[OSD([sQuery(id+"F7.wireOp",EDGE,"E67")])]})]});
            fillet(context, id + "F14", {"entities" : qUnion([Q0, Q1, Q2, Q3, Q4, Q5]), "radius" : 3 * mm, "tangentPropagation" : true, "allowEdgeOverflow" : false});
        }
        {
            var Q0;
            Q0=makeQuery(id+"F1.opExtrude","CAP_EDGE",EDGE,{"disambiguationData":[OSD([sQuery(id+"F0.wireOp",EDGE,"E1.bottom")])],"isStart":false});
            fillet(context, id + "F15", {"entities" : qUnion([Q0]), "radius" : 2 * mm, "tangentPropagation" : true, "allowEdgeOverflow" : false});
        }
        {
            var Q0;
            {var subQ0=sQuery(id+"F0.wireOp",EDGE,"E21.filletArc");var subQ1=sQuery(id+"F0.wireOp",EDGE,"E7");var subQ2=sQuery(id+"F0.wireOp",EDGE,"E6");var subQ3=sQuery(id+"F0.wireOp",EDGE,"E5");var subQ4=sQuery(id+"F0.wireOp",EDGE,"E4");var subQ5=sQuery(id+"F0.wireOp",EDGE,"E22.filletArc");var subQ6=sQuery(id+"F0.wireOp",EDGE,"E1.bottom");var subQ7=sQuery(id+"F0.wireOp",EDGE,"E1.right");var subQ8=sQuery(id+"F0.wireOp",EDGE,"E1.top");var subQ9=sQuery(id+"F0.wireOp",EDGE,"E1.left");var subQ10=sQuery(id+"F0.wireOp",EDGE,"E23.filletArc");var subQ11=sQuery(id+"F0.wireOp",EDGE,"E24.filletArc");Q0=makeQuery(id+"F2.boolean.opBoolean","SPLIT",FACE,{"disambiguationData":[TD([makeQuery(id+"F1.opExtrude","SWEPT_FACE",FACE,{"disambiguationData":[OSD([subQ6])]})])],"derivedFrom":makeQuery(id+"F1.opExtrude","CAP_FACE",FACE,{"disambiguationData":[OSD([subQ6,subQ8,subQ9,subQ7,subQ4,subQ3,subQ2,subQ1,subQ0,subQ5,subQ10,subQ11])],"isStart":true})});}
            var sketch = newSketch(context, id + "F16", { "sketchPlane" : qUnion([Q0])});
            skCircle(sketch, "E79.0", {"center": v(-60, 67.5) * mm, "radius": 4 * mm});
            skCircle(sketch, "E79.1", {"center": v(-60, -67.5) * mm, "radius": 4 * mm});
            skCircle(sketch, "E79.2", {"center": v(60, -67.5) * mm, "radius": 4 * mm});
            skCircle(sketch, "E79.3", {"center": v(60, 67.5) * mm, "radius": 4 * mm});
            skLineSegment(sketch, "E79.4", {"start": v(80, -80) * mm, "end": v(80, 80) * mm});
            skArc(sketch, "E79.5", {"start": v(80, 80) * mm, "mid": v(77.07, 87.07) * mm, "end": v(70, 90) * mm});
            skLineSegment(sketch, "E79.6", {"start": v(-70, 90) * mm, "end": v(70, 90) * mm});
            skArc(sketch, "E79.7", {"start": v(-70, 90) * mm, "mid": v(-77.07, 87.07) * mm, "end": v(-80, 80) * mm});
            skLineSegment(sketch, "E79.8", {"start": v(-80, -80) * mm, "end": v(-80, 80) * mm});
            skArc(sketch, "E79.9", {"start": v(-80, -80) * mm, "mid": v(-77.07, -87.07) * mm, "end": v(-70, -90) * mm});
            skLineSegment(sketch, "E79.10", {"start": v(-70, -90) * mm, "end": v(70, -90) * mm});
            skArc(sketch, "E79.11", {"start": v(70, -90) * mm, "mid": v(77.07, -87.07) * mm, "end": v(80, -80) * mm});
            skLineSegment(sketch, "E79.12", {"start": v(-60, 40.3) * mm, "end": v(-60, -40.3) * mm});
            skArc(sketch, "E79.13", {"start": v(56.15, 48.18) * mm, "mid": v(0, 67.5) * mm, "end": v(-56.15, 48.18) * mm});
            skLineSegment(sketch, "E79.14", {"start": v(60, 40.3) * mm, "end": v(60, -40.3) * mm});
            skArc(sketch, "E79.15", {"start": v(60, 40.3) * mm, "mid": v(58.99, 44.68) * mm, "end": v(56.15, 48.18) * mm});
            skArc(sketch, "E79.16", {"start": v(56.15, -48.18) * mm, "mid": v(58.99, -44.68) * mm, "end": v(60, -40.3) * mm});
            skArc(sketch, "E79.17", {"start": v(-56.15, -48.18) * mm, "mid": v(0, -67.5) * mm, "end": v(56.15, -48.18) * mm});
            skArc(sketch, "E79.18", {"start": v(-60, -40.3) * mm, "mid": v(-58.99, -44.68) * mm, "end": v(-56.15, -48.18) * mm});
            skArc(sketch, "E79.19", {"start": v(-56.15, 48.18) * mm, "mid": v(-58.99, 44.68) * mm, "end": v(-60, 40.3) * mm});
            skLineSegment(sketch, "E80", {"start": v(0, 23.75) * mm, "end": v(0, 120) * mm, "construction": true});
            skCircle(sketch, "E81", {"center": v(0, 120) * mm, "radius": 6 * mm});
            skArc(sketch, "E82", {"start": v(14.67, 123.1) * mm, "mid": v(0, 135) * mm, "end": v(-14.67, 123.1) * mm});
            skLineSegment(sketch, "E83", {"start": v(-14.67, 123.1) * mm, "end": v(-14.67, 108) * mm});
            skLineSegment(sketch, "E84", {"start": v(-14.67, 108) * mm, "end": v(-32.67, 90) * mm});
            skLineSegment(sketch, "E85", {"start": v(14.67, 123.1) * mm, "end": v(14.67, 108) * mm});
            skLineSegment(sketch, "E86", {"start": v(14.67, 108) * mm, "end": v(32.67, 90) * mm});
            skLineSegment(sketch, "E87", {"start": v(80, 0) * mm, "end": v(-80, 0) * mm, "construction": true});
            skLineSegment(sketch, "E88.MirrorCS", {"start": v(0, -23.75) * mm, "end": v(0, -120) * mm, "construction": true});
            skArc(sketch, "E89.MirrorCS", {"start": v(14.67, -123.1) * mm, "mid": v(0, -135) * mm, "end": v(-14.67, -123.1) * mm});
            skLineSegment(sketch, "E90.MirrorCS", {"start": v(-14.67, -108) * mm, "end": v(-32.67, -90) * mm});
            skLineSegment(sketch, "E91.MirrorCS", {"start": v(-60, -40.3) * mm, "end": v(-60, 40.3) * mm});
            skLineSegment(sketch, "E92.MirrorCS", {"start": v(-80, 80) * mm, "end": v(-80, -80) * mm});
            skArc(sketch, "E93.MirrorCS", {"start": v(-70, -90) * mm, "mid": v(-77.07, -87.07) * mm, "end": v(-80, -80) * mm});
            skArc(sketch, "E94.MirrorCS", {"start": v(80, -80) * mm, "mid": v(77.07, -87.07) * mm, "end": v(70, -90) * mm});
            skLineSegment(sketch, "E95.MirrorCS", {"start": v(80, 80) * mm, "end": v(80, -80) * mm});
            skArc(sketch, "E96.MirrorCS", {"start": v(60, -40.3) * mm, "mid": v(58.99, -44.68) * mm, "end": v(56.15, -48.18) * mm});
            skLineSegment(sketch, "E97.MirrorCS", {"start": v(60, -40.3) * mm, "end": v(60, 40.3) * mm});
            skLineSegment(sketch, "E98.MirrorCS", {"start": v(14.67, -108) * mm, "end": v(32.67, -90) * mm});
            skArc(sketch, "E99.MirrorCS", {"start": v(56.15, -48.18) * mm, "mid": v(0, -67.5) * mm, "end": v(-56.15, -48.18) * mm});
            skArc(sketch, "E100.MirrorCS", {"start": v(-56.15, -48.18) * mm, "mid": v(-58.99, -44.68) * mm, "end": v(-60, -40.3) * mm});
            skLineSegment(sketch, "E101.MirrorCS", {"start": v(14.67, -123.1) * mm, "end": v(14.67, -108) * mm});
            skCircle(sketch, "E102.MirrorC", {"center": v(0, -120) * mm, "radius": 6 * mm});
            skLineSegment(sketch, "E103.MirrorCS", {"start": v(-14.67, -123.1) * mm, "end": v(-14.67, -108) * mm});
            skSolve(sketch);
        }
        {
            var Q0;
            Q0=makeQuery(id+"F16.imprint","IMPRINT",FACE,{"disambiguationData":[TD([[makeQuery(id+"F16.imprint","IMPRINT",EDGE,{"derivedFrom":sQuery(id+"F16.wireOp",EDGE,"E81")}),-1.0]])]});
            var Q1;
            Q1=makeQuery(id+"F16.imprint","IMPRINT",FACE,{"disambiguationData":[TD([[makeQuery(id+"F16.imprint","IMPRINT",EDGE,{"derivedFrom":sQuery(id+"F16.wireOp",EDGE,"E79.0")}),-1.0]])]});
            var Q2;
            Q2=makeQuery(id+"F16.imprint","IMPRINT",FACE,{"disambiguationData":[TD([[makeQuery(id+"F16.imprint","IMPRINT",EDGE,{"derivedFrom":sQuery(id+"F16.wireOp",EDGE,"E89.MirrorCS")}),-1.0]])]});
            var Q3;
            Q3=makeQuery(id+"F2.opExtrude","CAP_FACE",FACE,{"disambiguationData":[OSD([sQuery(id+"F0.wireOp",EDGE,"E12"),sQuery(id+"F0.wireOp",EDGE,"E13"),sQuery(id+"F0.wireOp",EDGE,"E14"),sQuery(id+"F0.wireOp",EDGE,"E15"),sQuery(id+"F0.wireOp",EDGE,"E17.filletArc"),sQuery(id+"F0.wireOp",EDGE,"E18.filletArc"),sQuery(id+"F0.wireOp",EDGE,"E19.filletArc"),sQuery(id+"F0.wireOp",EDGE,"E20.filletArc"),sQuery(id+"F0.wireOp",EDGE,"E25.0"),sQuery(id+"F0.wireOp",EDGE,"E25.1"),sQuery(id+"F0.wireOp",EDGE,"E25.2"),sQuery(id+"F0.wireOp",EDGE,"E25.3"),sQuery(id+"F0.wireOp",EDGE,"E25.4"),sQuery(id+"F0.wireOp",EDGE,"E25.5"),sQuery(id+"F0.wireOp",EDGE,"E25.6"),sQuery(id+"F0.wireOp",EDGE,"E25.7")])],"isStart":false});
            extrude(context, id + "F17", {"entities" : qUnion([Q0, Q1, Q2]), "endBound" : BoundingType.UP_TO_SURFACE, "endBoundEntityFace" : qUnion([Q3]), "depth" : 25 * mm});
        }
    });
